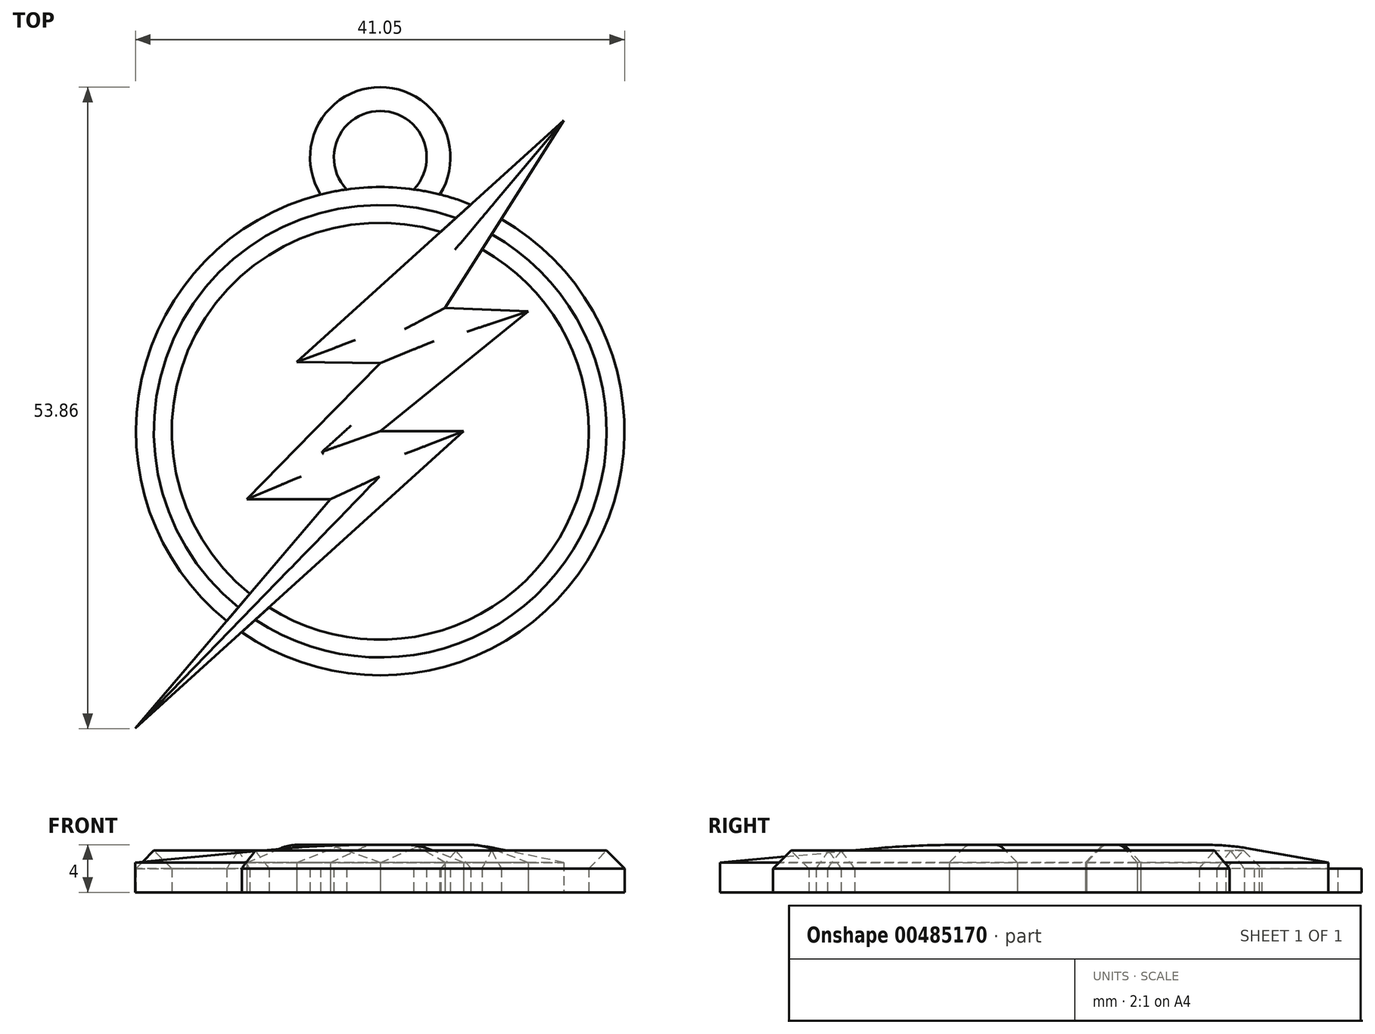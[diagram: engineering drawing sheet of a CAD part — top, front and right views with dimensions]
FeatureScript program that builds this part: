
annotation { "Feature Type Name" : "Feature", "Feature Type Description" : "" }
export const myFeature = defineFeature(function(context is Context, id is Id, definition is map)
    precondition{}
    {
        {
            var Q0;
            Q0=qCreatedBy(makeId("Top.planeOp"),FACE);
            var sketch = newSketch(context, id + "F0", { "sketchPlane" : qUnion([Q0])});
            skCircle(sketch, "E0", {"center": v(0, 0) * mm, "radius": 20.5 * mm});
            skCircle(sketch, "E1", {"center": v(0, 0) * mm, "radius": 17.5 * mm});
            skLineSegment(sketch, "E2", {"start": v(0, 0) * mm, "end": v(5.44, 4.4) * mm});
            skLineSegment(sketch, "E3", {"start": v(-5.6, 0) * mm, "end": v(-11.2, -5.71) * mm});
            skLineSegment(sketch, "E4", {"start": v(-11.2, -5.71) * mm, "end": v(-4.2, -5.71) * mm});
            skLineSegment(sketch, "E5", {"start": v(-4.2, -5.71) * mm, "end": v(-20.55, -24.97) * mm});
            skLineSegment(sketch, "E6", {"start": v(-20.55, -24.97) * mm, "end": v(7, 0) * mm});
            skLineSegment(sketch, "E7", {"start": v(7, 0) * mm, "end": v(0, 0) * mm});
            skLineSegment(sketch, "E8", {"start": v(5.44, 4.4) * mm, "end": v(12.43, 10.07) * mm});
            skLineSegment(sketch, "E9", {"start": v(12.43, 10.07) * mm, "end": v(5.44, 10.35) * mm});
            skLineSegment(sketch, "E10", {"start": v(5.44, 10.35) * mm, "end": v(15.4, 26.1) * mm});
            skLineSegment(sketch, "E11", {"start": v(15.4, 26.1) * mm, "end": v(-7, 5.8) * mm});
            skLineSegment(sketch, "E12", {"start": v(-7, 5.8) * mm, "end": v(0, 5.71) * mm});
            skLineSegment(sketch, "E13", {"start": v(0, 5.71) * mm, "end": v(-5.6, 0) * mm});
            skArc(sketch, "E14", {"start": v(5, 19.88) * mm, "mid": v(0, 28.9) * mm, "end": v(-5, 19.88) * mm});
            skArc(sketch, "E15.0", {"start": v(2.81, 20.3) * mm, "mid": v(0, 26.9) * mm, "end": v(-2.81, 20.3) * mm});
            skSolve(sketch);
        }
        {
            var Q0;
            {var subQ0=sQuery(id+"F0.wireOp",EDGE,"E11");var subQ1=sQuery(id+"F0.wireOp",EDGE,"E0");var subQ2=makeQuery(id+"F0.imprint","INTERSECT",VERTEX,{"derivedFrom":[subQ1,subQ0]});Q0=makeQuery(id+"F0.imprint","IMPRINT",FACE,{"disambiguationData":[TD([[makeQuery(id+"F0.imprint","IMPRINT",EDGE,{"disambiguationData":[TD([[subQ2,-1.0]])],"derivedFrom":subQ1}),1.0]])]});}
            var Q1;
            {var subQ0=sQuery(id+"F0.wireOp",EDGE,"E10");var subQ1=sQuery(id+"F0.wireOp",EDGE,"E0");var subQ2=makeQuery(id+"F0.imprint","INTERSECT",VERTEX,{"derivedFrom":[subQ1,subQ0]});Q1=makeQuery(id+"F0.imprint","IMPRINT",FACE,{"disambiguationData":[TD([[makeQuery(id+"F0.imprint","IMPRINT",EDGE,{"disambiguationData":[TD([[subQ2,1.0]])],"derivedFrom":subQ1}),1.0]])]});}
            extrude(context, id + "F1", {"entities" : qUnion([Q0, Q1]), "depth" : 4 * mm, "offsetDistance" : 25 * mm});
        }
        {
            var Q0;
            Q0=makeQuery(id+"F0.imprint","IMPRINT",FACE,{"disambiguationData":[TD([[makeQuery(id+"F0.imprint","IMPRINT",EDGE,{"derivedFrom":sQuery(id+"F0.wireOp",EDGE,"E3")}),-1.0]])]});
            var Q1;
            Q1=makeQuery(id+"F0.imprint","IMPRINT",FACE,{"disambiguationData":[TD([[makeQuery(id+"F0.imprint","IMPRINT",EDGE,{"derivedFrom":sQuery(id+"F0.wireOp",EDGE,"E2")}),-1.0]])]});
            extrude(context, id + "F2", {"entities" : qUnion([Q0, Q1]), "depth" : 2 * mm, "offsetDistance" : 25 * mm});
        }
        {
            var Q0;
            {var subQ0=sQuery(id+"F0.wireOp",EDGE,"E5");var subQ1=sQuery(id+"F0.wireOp",EDGE,"E0");var subQ2=makeQuery(id+"F0.imprint","INTERSECT",VERTEX,{"derivedFrom":[subQ1,subQ0]});Q0=makeQuery(id+"F0.imprint","IMPRINT",FACE,{"disambiguationData":[TD([[makeQuery(id+"F0.imprint","IMPRINT",EDGE,{"disambiguationData":[TD([[subQ2,-1.0]])],"derivedFrom":subQ1}),-1.0]])]});}
            var Q1;
            {var subQ0=sQuery(id+"F0.wireOp",EDGE,"E5");var subQ1=sQuery(id+"F0.wireOp",EDGE,"E0");var subQ2=makeQuery(id+"F0.imprint","INTERSECT",VERTEX,{"derivedFrom":[subQ1,subQ0]});Q1=makeQuery(id+"F0.imprint","IMPRINT",FACE,{"disambiguationData":[TD([[makeQuery(id+"F0.imprint","IMPRINT",EDGE,{"disambiguationData":[TD([[subQ2,-1.0]])],"derivedFrom":subQ1}),1.0]])]});}
            var Q2;
            Q2=makeQuery(id+"F0.imprint","IMPRINT",FACE,{"disambiguationData":[TD([[makeQuery(id+"F0.imprint","IMPRINT",EDGE,{"derivedFrom":sQuery(id+"F0.wireOp",EDGE,"E2")}),1.0]])]});
            var Q3;
            {var subQ0=sQuery(id+"F0.wireOp",EDGE,"E11");var subQ1=sQuery(id+"F0.wireOp",EDGE,"E0");var subQ2=makeQuery(id+"F0.imprint","INTERSECT",VERTEX,{"derivedFrom":[subQ1,subQ0]});Q3=makeQuery(id+"F0.imprint","IMPRINT",FACE,{"disambiguationData":[TD([[makeQuery(id+"F0.imprint","IMPRINT",EDGE,{"disambiguationData":[TD([[subQ2,1.0]])],"derivedFrom":subQ1}),1.0]])]});}
            var Q4;
            {var subQ0=sQuery(id+"F0.wireOp",EDGE,"E11");var subQ1=sQuery(id+"F0.wireOp",EDGE,"E0");var subQ2=makeQuery(id+"F0.imprint","INTERSECT",VERTEX,{"derivedFrom":[subQ1,subQ0]});Q4=makeQuery(id+"F0.imprint","IMPRINT",FACE,{"disambiguationData":[TD([[makeQuery(id+"F0.imprint","IMPRINT",EDGE,{"disambiguationData":[TD([[subQ2,1.0]])],"derivedFrom":subQ1}),-1.0]])]});}
            extrude(context, id + "F3", {"entities" : qUnion([Q0, Q1, Q2, Q3, Q4]), "depth" : 4 * mm, "offsetDistance" : 25 * mm});
        }
        {
            var Q0;
            {var subQ0=sQuery(id+"F0.wireOp",EDGE,"E1");Q0=makeQuery(id+"F1.opExtrude","CAP_EDGE",EDGE,{"disambiguationData":[OSD([subQ0]),TDD([makeQuery(id+"F0.imprint","IMPRINT",EDGE,{"disambiguationData":[TD([[makeQuery(id+"F0.imprint","INTERSECT",VERTEX,{"derivedFrom":[subQ0,sQuery(id+"F0.wireOp",EDGE,"E10")]}),1.0]])],"derivedFrom":subQ0})])],"isStart":false});}
            var Q1;
            {var subQ0=sQuery(id+"F0.wireOp",EDGE,"E0");Q1=makeQuery(id+"F1.opExtrude","CAP_EDGE",EDGE,{"disambiguationData":[OSD([subQ0]),TDD([makeQuery(id+"F0.imprint","IMPRINT",EDGE,{"disambiguationData":[TD([[makeQuery(id+"F0.imprint","INTERSECT",VERTEX,{"derivedFrom":[subQ0,sQuery(id+"F0.wireOp",EDGE,"E10")]}),1.0]])],"derivedFrom":subQ0})])],"isStart":false});}
            var Q2;
            {var subQ0=sQuery(id+"F0.wireOp",EDGE,"E1");Q2=makeQuery(id+"F1.opExtrude","CAP_EDGE",EDGE,{"disambiguationData":[OSD([subQ0]),TDD([makeQuery(id+"F0.imprint","IMPRINT",EDGE,{"disambiguationData":[TD([[makeQuery(id+"F0.imprint","INTERSECT",VERTEX,{"derivedFrom":[subQ0,sQuery(id+"F0.wireOp",EDGE,"E11")]}),-1.0]])],"derivedFrom":subQ0})])],"isStart":false});}
            var Q3;
            {var subQ0=sQuery(id+"F0.wireOp",EDGE,"E0");Q3=makeQuery(id+"F1.opExtrude","CAP_EDGE",EDGE,{"disambiguationData":[OSD([subQ0]),TDD([makeQuery(id+"F0.imprint","IMPRINT",EDGE,{"disambiguationData":[TD([[makeQuery(id+"F0.imprint","INTERSECT",VERTEX,{"derivedFrom":[subQ0,sQuery(id+"F0.wireOp",EDGE,"E11")]}),-1.0]])],"derivedFrom":subQ0})])],"isStart":false});}
            chamfer(context, id + "F4", {"entities" : qUnion([Q0, Q1, Q2, Q3]), "width" : 2 * mm, "tangentPropagation" : true});
        }
        {
            var Q0;
            Q0=makeQuery(id+"F3.opExtrude","CAP_EDGE",EDGE,{"disambiguationData":[OSD([sQuery(id+"F0.wireOp",EDGE,"E6")])],"isStart":false});
            var Q1;
            Q1=makeQuery(id+"F3.opExtrude","CAP_EDGE",EDGE,{"disambiguationData":[OSD([sQuery(id+"F0.wireOp",EDGE,"E5")])],"isStart":false});
            var Q2;
            Q2=makeQuery(id+"F3.opExtrude","CAP_EDGE",EDGE,{"disambiguationData":[OSD([sQuery(id+"F0.wireOp",EDGE,"E4")])],"isStart":false});
            var Q3;
            Q3=makeQuery(id+"F3.opExtrude","CAP_EDGE",EDGE,{"disambiguationData":[OSD([sQuery(id+"F0.wireOp",EDGE,"E3")])],"isStart":false});
            var Q4;
            Q4=makeQuery(id+"F3.opExtrude","CAP_EDGE",EDGE,{"disambiguationData":[OSD([sQuery(id+"F0.wireOp",EDGE,"E13")])],"isStart":false});
            var Q5;
            Q5=makeQuery(id+"F3.opExtrude","CAP_EDGE",EDGE,{"disambiguationData":[OSD([sQuery(id+"F0.wireOp",EDGE,"E7")])],"isStart":false});
            var Q6;
            Q6=makeQuery(id+"F3.opExtrude","CAP_EDGE",EDGE,{"disambiguationData":[OSD([sQuery(id+"F0.wireOp",EDGE,"E2"),sQuery(id+"F0.wireOp",EDGE,"E8")])],"isStart":false});
            var Q7;
            Q7=makeQuery(id+"F3.opExtrude","CAP_EDGE",EDGE,{"disambiguationData":[OSD([sQuery(id+"F0.wireOp",EDGE,"E9")])],"isStart":false});
            var Q8;
            Q8=makeQuery(id+"F3.opExtrude","CAP_EDGE",EDGE,{"disambiguationData":[OSD([sQuery(id+"F0.wireOp",EDGE,"E12")])],"isStart":false});
            var Q9;
            Q9=makeQuery(id+"F3.opExtrude","CAP_EDGE",EDGE,{"disambiguationData":[OSD([sQuery(id+"F0.wireOp",EDGE,"E11")])],"isStart":false});
            var Q10;
            Q10=makeQuery(id+"F3.opExtrude","CAP_EDGE",EDGE,{"disambiguationData":[OSD([sQuery(id+"F0.wireOp",EDGE,"E10")])],"isStart":false});
            chamfer(context, id + "F5", {"entities" : qUnion([Q0, Q1, Q2, Q3, Q4, Q5, Q6, Q7, Q8, Q9, Q10]), "width" : 1.5 * mm, "tangentPropagation" : true});
        }
        {
            var Q0;
            {var subQ0=sQuery(id+"F0.wireOp",EDGE,"E11");Q0=makeQuery(id+"F5.opChamfer","BLEND_EDGE",EDGE,{"blendedFrom":[makeQuery(id+"F3.opExtrude","CAP_EDGE",EDGE,{"disambiguationData":[OSD([subQ0])],"isStart":false}),makeQuery(id+"F3.opExtrude","CAP_FACE",FACE,{"disambiguationData":[OSD([sQuery(id+"F0.wireOp",EDGE,"E2"),sQuery(id+"F0.wireOp",EDGE,"E3"),sQuery(id+"F0.wireOp",EDGE,"E4"),sQuery(id+"F0.wireOp",EDGE,"E5"),sQuery(id+"F0.wireOp",EDGE,"E6"),sQuery(id+"F0.wireOp",EDGE,"E7"),sQuery(id+"F0.wireOp",EDGE,"E8"),sQuery(id+"F0.wireOp",EDGE,"E9"),sQuery(id+"F0.wireOp",EDGE,"E10"),subQ0,sQuery(id+"F0.wireOp",EDGE,"E12"),sQuery(id+"F0.wireOp",EDGE,"E13")])],"isStart":false})],"blendedInto":[makeQuery(id+"F3.opExtrude","CAP_FACE",FACE,{"disambiguationData":[OSD([sQuery(id+"F0.wireOp",EDGE,"E2"),sQuery(id+"F0.wireOp",EDGE,"E3"),sQuery(id+"F0.wireOp",EDGE,"E4"),sQuery(id+"F0.wireOp",EDGE,"E5"),sQuery(id+"F0.wireOp",EDGE,"E6"),sQuery(id+"F0.wireOp",EDGE,"E7"),sQuery(id+"F0.wireOp",EDGE,"E8"),sQuery(id+"F0.wireOp",EDGE,"E9"),sQuery(id+"F0.wireOp",EDGE,"E10"),subQ0,sQuery(id+"F0.wireOp",EDGE,"E12"),sQuery(id+"F0.wireOp",EDGE,"E13")])],"isStart":false})]});}
            var Q1;
            {var subQ0=sQuery(id+"F0.wireOp",EDGE,"E10");Q1=makeQuery(id+"F5.opChamfer","BLEND_EDGE",EDGE,{"blendedFrom":[makeQuery(id+"F3.opExtrude","CAP_EDGE",EDGE,{"disambiguationData":[OSD([subQ0])],"isStart":false}),makeQuery(id+"F3.opExtrude","CAP_FACE",FACE,{"disambiguationData":[OSD([sQuery(id+"F0.wireOp",EDGE,"E2"),sQuery(id+"F0.wireOp",EDGE,"E3"),sQuery(id+"F0.wireOp",EDGE,"E4"),sQuery(id+"F0.wireOp",EDGE,"E5"),sQuery(id+"F0.wireOp",EDGE,"E6"),sQuery(id+"F0.wireOp",EDGE,"E7"),sQuery(id+"F0.wireOp",EDGE,"E8"),sQuery(id+"F0.wireOp",EDGE,"E9"),subQ0,sQuery(id+"F0.wireOp",EDGE,"E11"),sQuery(id+"F0.wireOp",EDGE,"E12"),sQuery(id+"F0.wireOp",EDGE,"E13")])],"isStart":false})],"blendedInto":[makeQuery(id+"F3.opExtrude","CAP_FACE",FACE,{"disambiguationData":[OSD([sQuery(id+"F0.wireOp",EDGE,"E2"),sQuery(id+"F0.wireOp",EDGE,"E3"),sQuery(id+"F0.wireOp",EDGE,"E4"),sQuery(id+"F0.wireOp",EDGE,"E5"),sQuery(id+"F0.wireOp",EDGE,"E6"),sQuery(id+"F0.wireOp",EDGE,"E7"),sQuery(id+"F0.wireOp",EDGE,"E8"),sQuery(id+"F0.wireOp",EDGE,"E9"),subQ0,sQuery(id+"F0.wireOp",EDGE,"E11"),sQuery(id+"F0.wireOp",EDGE,"E12"),sQuery(id+"F0.wireOp",EDGE,"E13")])],"isStart":false})]});}
            var Q2;
            {var subQ0=sQuery(id+"F0.wireOp",EDGE,"E9");Q2=makeQuery(id+"F5.opChamfer","BLEND_EDGE",EDGE,{"blendedFrom":[makeQuery(id+"F3.opExtrude","CAP_EDGE",EDGE,{"disambiguationData":[OSD([subQ0])],"isStart":false}),makeQuery(id+"F3.opExtrude","CAP_FACE",FACE,{"disambiguationData":[OSD([sQuery(id+"F0.wireOp",EDGE,"E2"),sQuery(id+"F0.wireOp",EDGE,"E3"),sQuery(id+"F0.wireOp",EDGE,"E4"),sQuery(id+"F0.wireOp",EDGE,"E5"),sQuery(id+"F0.wireOp",EDGE,"E6"),sQuery(id+"F0.wireOp",EDGE,"E7"),sQuery(id+"F0.wireOp",EDGE,"E8"),subQ0,sQuery(id+"F0.wireOp",EDGE,"E10"),sQuery(id+"F0.wireOp",EDGE,"E11"),sQuery(id+"F0.wireOp",EDGE,"E12"),sQuery(id+"F0.wireOp",EDGE,"E13")])],"isStart":false})],"blendedInto":[makeQuery(id+"F3.opExtrude","CAP_FACE",FACE,{"disambiguationData":[OSD([sQuery(id+"F0.wireOp",EDGE,"E2"),sQuery(id+"F0.wireOp",EDGE,"E3"),sQuery(id+"F0.wireOp",EDGE,"E4"),sQuery(id+"F0.wireOp",EDGE,"E5"),sQuery(id+"F0.wireOp",EDGE,"E6"),sQuery(id+"F0.wireOp",EDGE,"E7"),sQuery(id+"F0.wireOp",EDGE,"E8"),subQ0,sQuery(id+"F0.wireOp",EDGE,"E10"),sQuery(id+"F0.wireOp",EDGE,"E11"),sQuery(id+"F0.wireOp",EDGE,"E12"),sQuery(id+"F0.wireOp",EDGE,"E13")])],"isStart":false})]});}
            var Q3;
            {var subQ0=sQuery(id+"F0.wireOp",EDGE,"E12");Q3=makeQuery(id+"F5.opChamfer","BLEND_EDGE",EDGE,{"blendedFrom":[makeQuery(id+"F3.opExtrude","CAP_EDGE",EDGE,{"disambiguationData":[OSD([subQ0])],"isStart":false}),makeQuery(id+"F3.opExtrude","CAP_FACE",FACE,{"disambiguationData":[OSD([sQuery(id+"F0.wireOp",EDGE,"E2"),sQuery(id+"F0.wireOp",EDGE,"E3"),sQuery(id+"F0.wireOp",EDGE,"E4"),sQuery(id+"F0.wireOp",EDGE,"E5"),sQuery(id+"F0.wireOp",EDGE,"E6"),sQuery(id+"F0.wireOp",EDGE,"E7"),sQuery(id+"F0.wireOp",EDGE,"E8"),sQuery(id+"F0.wireOp",EDGE,"E9"),sQuery(id+"F0.wireOp",EDGE,"E10"),sQuery(id+"F0.wireOp",EDGE,"E11"),subQ0,sQuery(id+"F0.wireOp",EDGE,"E13")])],"isStart":false})],"blendedInto":[makeQuery(id+"F3.opExtrude","CAP_FACE",FACE,{"disambiguationData":[OSD([sQuery(id+"F0.wireOp",EDGE,"E2"),sQuery(id+"F0.wireOp",EDGE,"E3"),sQuery(id+"F0.wireOp",EDGE,"E4"),sQuery(id+"F0.wireOp",EDGE,"E5"),sQuery(id+"F0.wireOp",EDGE,"E6"),sQuery(id+"F0.wireOp",EDGE,"E7"),sQuery(id+"F0.wireOp",EDGE,"E8"),sQuery(id+"F0.wireOp",EDGE,"E9"),sQuery(id+"F0.wireOp",EDGE,"E10"),sQuery(id+"F0.wireOp",EDGE,"E11"),subQ0,sQuery(id+"F0.wireOp",EDGE,"E13")])],"isStart":false})]});}
            var Q4;
            {var subQ0=sQuery(id+"F0.wireOp",EDGE,"E13");Q4=makeQuery(id+"F5.opChamfer","BLEND_EDGE",EDGE,{"blendedFrom":[makeQuery(id+"F3.opExtrude","CAP_EDGE",EDGE,{"disambiguationData":[OSD([subQ0])],"isStart":false}),makeQuery(id+"F3.opExtrude","CAP_FACE",FACE,{"disambiguationData":[OSD([sQuery(id+"F0.wireOp",EDGE,"E2"),sQuery(id+"F0.wireOp",EDGE,"E3"),sQuery(id+"F0.wireOp",EDGE,"E4"),sQuery(id+"F0.wireOp",EDGE,"E5"),sQuery(id+"F0.wireOp",EDGE,"E6"),sQuery(id+"F0.wireOp",EDGE,"E7"),sQuery(id+"F0.wireOp",EDGE,"E8"),sQuery(id+"F0.wireOp",EDGE,"E9"),sQuery(id+"F0.wireOp",EDGE,"E10"),sQuery(id+"F0.wireOp",EDGE,"E11"),sQuery(id+"F0.wireOp",EDGE,"E12"),subQ0])],"isStart":false})],"blendedInto":[makeQuery(id+"F3.opExtrude","CAP_FACE",FACE,{"disambiguationData":[OSD([sQuery(id+"F0.wireOp",EDGE,"E2"),sQuery(id+"F0.wireOp",EDGE,"E3"),sQuery(id+"F0.wireOp",EDGE,"E4"),sQuery(id+"F0.wireOp",EDGE,"E5"),sQuery(id+"F0.wireOp",EDGE,"E6"),sQuery(id+"F0.wireOp",EDGE,"E7"),sQuery(id+"F0.wireOp",EDGE,"E8"),sQuery(id+"F0.wireOp",EDGE,"E9"),sQuery(id+"F0.wireOp",EDGE,"E10"),sQuery(id+"F0.wireOp",EDGE,"E11"),sQuery(id+"F0.wireOp",EDGE,"E12"),subQ0])],"isStart":false})]});}
            var Q5;
            {var subQ0=sQuery(id+"F0.wireOp",EDGE,"E8");var subQ1=sQuery(id+"F0.wireOp",EDGE,"E2");Q5=makeQuery(id+"F5.opChamfer","BLEND_EDGE",EDGE,{"blendedFrom":[makeQuery(id+"F3.opExtrude","CAP_EDGE",EDGE,{"disambiguationData":[OSD([subQ1,subQ0])],"isStart":false}),makeQuery(id+"F3.opExtrude","CAP_FACE",FACE,{"disambiguationData":[OSD([subQ1,sQuery(id+"F0.wireOp",EDGE,"E3"),sQuery(id+"F0.wireOp",EDGE,"E4"),sQuery(id+"F0.wireOp",EDGE,"E5"),sQuery(id+"F0.wireOp",EDGE,"E6"),sQuery(id+"F0.wireOp",EDGE,"E7"),subQ0,sQuery(id+"F0.wireOp",EDGE,"E9"),sQuery(id+"F0.wireOp",EDGE,"E10"),sQuery(id+"F0.wireOp",EDGE,"E11"),sQuery(id+"F0.wireOp",EDGE,"E12"),sQuery(id+"F0.wireOp",EDGE,"E13")])],"isStart":false})],"blendedInto":[makeQuery(id+"F3.opExtrude","CAP_FACE",FACE,{"disambiguationData":[OSD([subQ1,sQuery(id+"F0.wireOp",EDGE,"E3"),sQuery(id+"F0.wireOp",EDGE,"E4"),sQuery(id+"F0.wireOp",EDGE,"E5"),sQuery(id+"F0.wireOp",EDGE,"E6"),sQuery(id+"F0.wireOp",EDGE,"E7"),subQ0,sQuery(id+"F0.wireOp",EDGE,"E9"),sQuery(id+"F0.wireOp",EDGE,"E10"),sQuery(id+"F0.wireOp",EDGE,"E11"),sQuery(id+"F0.wireOp",EDGE,"E12"),sQuery(id+"F0.wireOp",EDGE,"E13")])],"isStart":false})]});}
            var Q6;
            {var subQ0=sQuery(id+"F0.wireOp",EDGE,"E7");Q6=makeQuery(id+"F5.opChamfer","BLEND_EDGE",EDGE,{"blendedFrom":[makeQuery(id+"F3.opExtrude","CAP_EDGE",EDGE,{"disambiguationData":[OSD([subQ0])],"isStart":false}),makeQuery(id+"F3.opExtrude","CAP_FACE",FACE,{"disambiguationData":[OSD([sQuery(id+"F0.wireOp",EDGE,"E2"),sQuery(id+"F0.wireOp",EDGE,"E3"),sQuery(id+"F0.wireOp",EDGE,"E4"),sQuery(id+"F0.wireOp",EDGE,"E5"),sQuery(id+"F0.wireOp",EDGE,"E6"),subQ0,sQuery(id+"F0.wireOp",EDGE,"E8"),sQuery(id+"F0.wireOp",EDGE,"E9"),sQuery(id+"F0.wireOp",EDGE,"E10"),sQuery(id+"F0.wireOp",EDGE,"E11"),sQuery(id+"F0.wireOp",EDGE,"E12"),sQuery(id+"F0.wireOp",EDGE,"E13")])],"isStart":false})],"blendedInto":[makeQuery(id+"F3.opExtrude","CAP_FACE",FACE,{"disambiguationData":[OSD([sQuery(id+"F0.wireOp",EDGE,"E2"),sQuery(id+"F0.wireOp",EDGE,"E3"),sQuery(id+"F0.wireOp",EDGE,"E4"),sQuery(id+"F0.wireOp",EDGE,"E5"),sQuery(id+"F0.wireOp",EDGE,"E6"),subQ0,sQuery(id+"F0.wireOp",EDGE,"E8"),sQuery(id+"F0.wireOp",EDGE,"E9"),sQuery(id+"F0.wireOp",EDGE,"E10"),sQuery(id+"F0.wireOp",EDGE,"E11"),sQuery(id+"F0.wireOp",EDGE,"E12"),sQuery(id+"F0.wireOp",EDGE,"E13")])],"isStart":false})]});}
            var Q7;
            {var subQ0=sQuery(id+"F0.wireOp",EDGE,"E6");Q7=makeQuery(id+"F5.opChamfer","BLEND_EDGE",EDGE,{"blendedFrom":[makeQuery(id+"F3.opExtrude","CAP_EDGE",EDGE,{"disambiguationData":[OSD([subQ0])],"isStart":false}),makeQuery(id+"F3.opExtrude","CAP_FACE",FACE,{"disambiguationData":[OSD([sQuery(id+"F0.wireOp",EDGE,"E2"),sQuery(id+"F0.wireOp",EDGE,"E3"),sQuery(id+"F0.wireOp",EDGE,"E4"),sQuery(id+"F0.wireOp",EDGE,"E5"),subQ0,sQuery(id+"F0.wireOp",EDGE,"E7"),sQuery(id+"F0.wireOp",EDGE,"E8"),sQuery(id+"F0.wireOp",EDGE,"E9"),sQuery(id+"F0.wireOp",EDGE,"E10"),sQuery(id+"F0.wireOp",EDGE,"E11"),sQuery(id+"F0.wireOp",EDGE,"E12"),sQuery(id+"F0.wireOp",EDGE,"E13")])],"isStart":false})],"blendedInto":[makeQuery(id+"F3.opExtrude","CAP_FACE",FACE,{"disambiguationData":[OSD([sQuery(id+"F0.wireOp",EDGE,"E2"),sQuery(id+"F0.wireOp",EDGE,"E3"),sQuery(id+"F0.wireOp",EDGE,"E4"),sQuery(id+"F0.wireOp",EDGE,"E5"),subQ0,sQuery(id+"F0.wireOp",EDGE,"E7"),sQuery(id+"F0.wireOp",EDGE,"E8"),sQuery(id+"F0.wireOp",EDGE,"E9"),sQuery(id+"F0.wireOp",EDGE,"E10"),sQuery(id+"F0.wireOp",EDGE,"E11"),sQuery(id+"F0.wireOp",EDGE,"E12"),sQuery(id+"F0.wireOp",EDGE,"E13")])],"isStart":false})]});}
            var Q8;
            {var subQ0=sQuery(id+"F0.wireOp",EDGE,"E4");Q8=makeQuery(id+"F5.opChamfer","BLEND_EDGE",EDGE,{"blendedFrom":[makeQuery(id+"F3.opExtrude","CAP_EDGE",EDGE,{"disambiguationData":[OSD([subQ0])],"isStart":false}),makeQuery(id+"F3.opExtrude","CAP_FACE",FACE,{"disambiguationData":[OSD([sQuery(id+"F0.wireOp",EDGE,"E2"),sQuery(id+"F0.wireOp",EDGE,"E3"),subQ0,sQuery(id+"F0.wireOp",EDGE,"E5"),sQuery(id+"F0.wireOp",EDGE,"E6"),sQuery(id+"F0.wireOp",EDGE,"E7"),sQuery(id+"F0.wireOp",EDGE,"E8"),sQuery(id+"F0.wireOp",EDGE,"E9"),sQuery(id+"F0.wireOp",EDGE,"E10"),sQuery(id+"F0.wireOp",EDGE,"E11"),sQuery(id+"F0.wireOp",EDGE,"E12"),sQuery(id+"F0.wireOp",EDGE,"E13")])],"isStart":false})],"blendedInto":[makeQuery(id+"F3.opExtrude","CAP_FACE",FACE,{"disambiguationData":[OSD([sQuery(id+"F0.wireOp",EDGE,"E2"),sQuery(id+"F0.wireOp",EDGE,"E3"),subQ0,sQuery(id+"F0.wireOp",EDGE,"E5"),sQuery(id+"F0.wireOp",EDGE,"E6"),sQuery(id+"F0.wireOp",EDGE,"E7"),sQuery(id+"F0.wireOp",EDGE,"E8"),sQuery(id+"F0.wireOp",EDGE,"E9"),sQuery(id+"F0.wireOp",EDGE,"E10"),sQuery(id+"F0.wireOp",EDGE,"E11"),sQuery(id+"F0.wireOp",EDGE,"E12"),sQuery(id+"F0.wireOp",EDGE,"E13")])],"isStart":false})]});}
            var Q9;
            {var subQ0=sQuery(id+"F0.wireOp",EDGE,"E5");Q9=makeQuery(id+"F5.opChamfer","BLEND_EDGE",EDGE,{"blendedFrom":[makeQuery(id+"F3.opExtrude","CAP_EDGE",EDGE,{"disambiguationData":[OSD([subQ0])],"isStart":false}),makeQuery(id+"F3.opExtrude","CAP_FACE",FACE,{"disambiguationData":[OSD([sQuery(id+"F0.wireOp",EDGE,"E2"),sQuery(id+"F0.wireOp",EDGE,"E3"),sQuery(id+"F0.wireOp",EDGE,"E4"),subQ0,sQuery(id+"F0.wireOp",EDGE,"E6"),sQuery(id+"F0.wireOp",EDGE,"E7"),sQuery(id+"F0.wireOp",EDGE,"E8"),sQuery(id+"F0.wireOp",EDGE,"E9"),sQuery(id+"F0.wireOp",EDGE,"E10"),sQuery(id+"F0.wireOp",EDGE,"E11"),sQuery(id+"F0.wireOp",EDGE,"E12"),sQuery(id+"F0.wireOp",EDGE,"E13")])],"isStart":false})],"blendedInto":[makeQuery(id+"F3.opExtrude","CAP_FACE",FACE,{"disambiguationData":[OSD([sQuery(id+"F0.wireOp",EDGE,"E2"),sQuery(id+"F0.wireOp",EDGE,"E3"),sQuery(id+"F0.wireOp",EDGE,"E4"),subQ0,sQuery(id+"F0.wireOp",EDGE,"E6"),sQuery(id+"F0.wireOp",EDGE,"E7"),sQuery(id+"F0.wireOp",EDGE,"E8"),sQuery(id+"F0.wireOp",EDGE,"E9"),sQuery(id+"F0.wireOp",EDGE,"E10"),sQuery(id+"F0.wireOp",EDGE,"E11"),sQuery(id+"F0.wireOp",EDGE,"E12"),sQuery(id+"F0.wireOp",EDGE,"E13")])],"isStart":false})]});}
            var Q10;
            {var subQ0=sQuery(id+"F0.wireOp",EDGE,"E3");Q10=makeQuery(id+"F5.opChamfer","BLEND_EDGE",EDGE,{"blendedFrom":[makeQuery(id+"F3.opExtrude","CAP_EDGE",EDGE,{"disambiguationData":[OSD([subQ0])],"isStart":false}),makeQuery(id+"F3.opExtrude","CAP_FACE",FACE,{"disambiguationData":[OSD([sQuery(id+"F0.wireOp",EDGE,"E2"),subQ0,sQuery(id+"F0.wireOp",EDGE,"E4"),sQuery(id+"F0.wireOp",EDGE,"E5"),sQuery(id+"F0.wireOp",EDGE,"E6"),sQuery(id+"F0.wireOp",EDGE,"E7"),sQuery(id+"F0.wireOp",EDGE,"E8"),sQuery(id+"F0.wireOp",EDGE,"E9"),sQuery(id+"F0.wireOp",EDGE,"E10"),sQuery(id+"F0.wireOp",EDGE,"E11"),sQuery(id+"F0.wireOp",EDGE,"E12"),sQuery(id+"F0.wireOp",EDGE,"E13")])],"isStart":false})],"blendedInto":[makeQuery(id+"F3.opExtrude","CAP_FACE",FACE,{"disambiguationData":[OSD([sQuery(id+"F0.wireOp",EDGE,"E2"),subQ0,sQuery(id+"F0.wireOp",EDGE,"E4"),sQuery(id+"F0.wireOp",EDGE,"E5"),sQuery(id+"F0.wireOp",EDGE,"E6"),sQuery(id+"F0.wireOp",EDGE,"E7"),sQuery(id+"F0.wireOp",EDGE,"E8"),sQuery(id+"F0.wireOp",EDGE,"E9"),sQuery(id+"F0.wireOp",EDGE,"E10"),sQuery(id+"F0.wireOp",EDGE,"E11"),sQuery(id+"F0.wireOp",EDGE,"E12"),sQuery(id+"F0.wireOp",EDGE,"E13")])],"isStart":false})]});}
            fillet(context, id + "F6", {"entities" : qUnion([Q0, Q1, Q2, Q3, Q4, Q5, Q6, Q7, Q8, Q9, Q10]), "radius" : 1 * mm, "tangentPropagation" : true, "allowEdgeOverflow" : false});
        }
        {
            var Q0;
            {var subQ0=sQuery(id+"F0.wireOp",EDGE,"E14");Q0=makeQuery(id+"F0.imprint","IMPRINT",FACE,{"disambiguationData":[TD([[makeQuery(id+"F0.imprint","IMPRINT",EDGE,{"derivedFrom":subQ0}),1.0]])]});}
            extrude(context, id + "F7", {"entities" : qUnion([Q0]), "operationType" : NewBodyOperationType.ADD, "depth" : 2 * mm, "offsetDistance" : 25 * mm});
        }
    });
